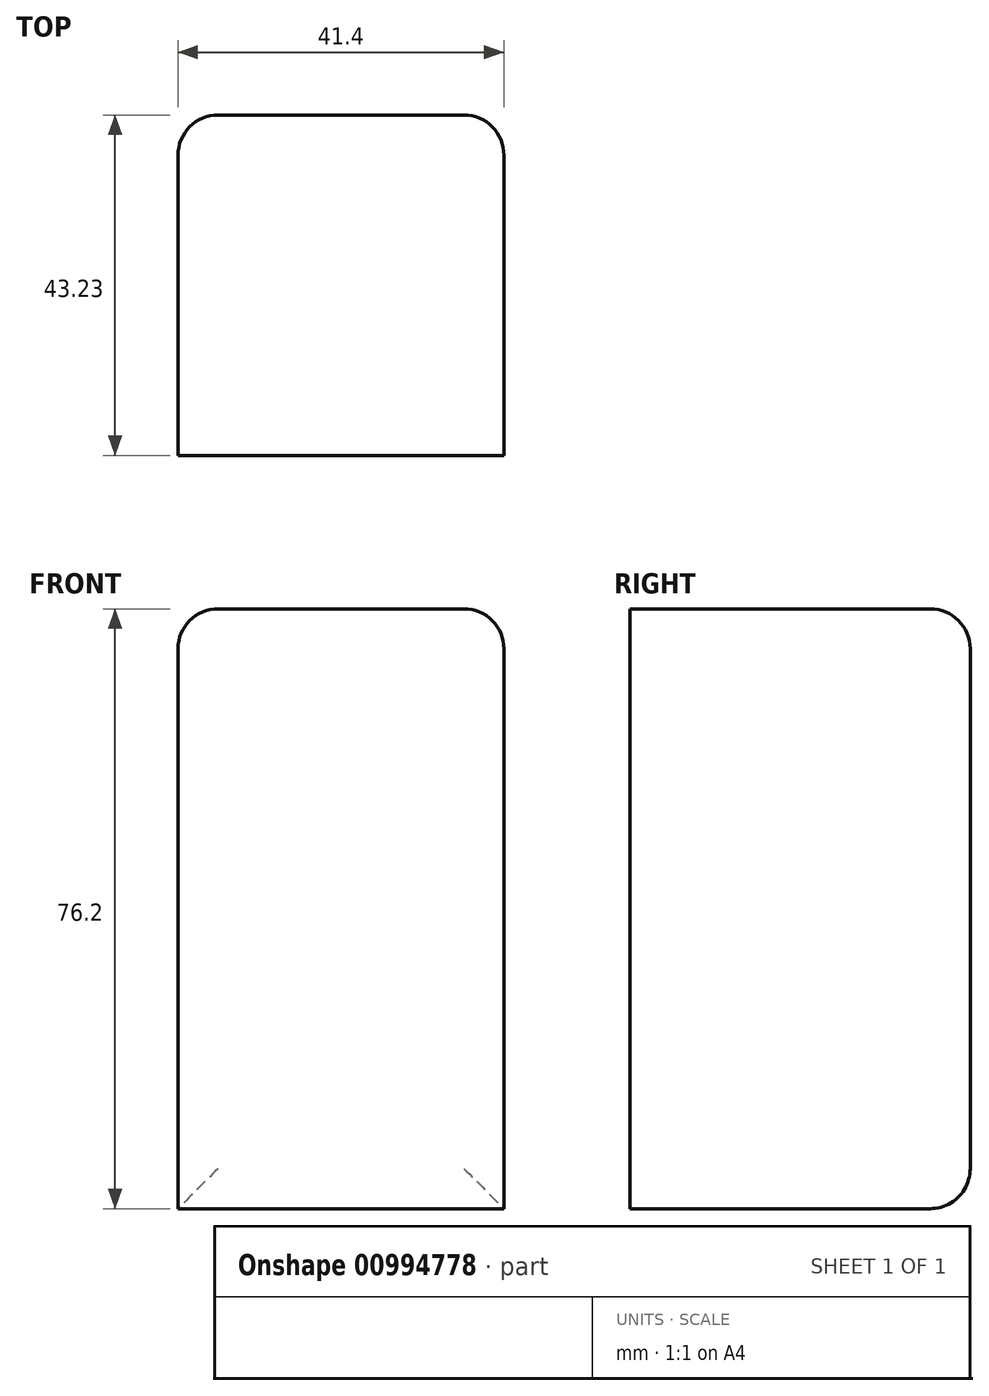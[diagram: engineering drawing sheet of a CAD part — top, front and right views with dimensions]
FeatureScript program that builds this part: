
annotation { "Feature Type Name" : "Feature", "Feature Type Description" : "" }
export const myFeature = defineFeature(function(context is Context, id is Id, definition is map)
    precondition{}
    {
        {
            var Q0;
            Q0=qCreatedBy(makeId("Top.planeOp"),FACE);
            var sketch = newSketch(context, id + "F0", { "sketchPlane" : qUnion([Q0])});
            skLineSegment(sketch, "E0.bottom", {"start": v(0, 56.88) * mm, "end": v(41.4, 56.88) * mm});
            skLineSegment(sketch, "E0.top", {"start": v(0, 13.65) * mm, "end": v(41.4, 13.65) * mm});
            skLineSegment(sketch, "E0.left", {"start": v(0, 56.88) * mm, "end": v(0, 13.65) * mm});
            skLineSegment(sketch, "E0.right", {"start": v(41.4, 56.88) * mm, "end": v(41.4, 13.65) * mm});
            skSolve(sketch);
        }
        {
            var Q0;
            Q0=makeQuery(id+"F0.imprint","IMPRINT",FACE,{"disambiguationData":[TD([[makeQuery(id+"F0.imprint","IMPRINT",EDGE,{"derivedFrom":sQuery(id+"F0.wireOp",EDGE,"E0.bottom")}),-1.0]])]});
            extrude(context, id + "F1", {"entities" : qUnion([Q0]), "depth" : 76.2 * mm, "offsetDistance" : 25.4 * mm});
        }
        {
            var Q0;
            Q0=makeQuery(id+"F1.opExtrude","SWEPT_FACE",FACE,{"disambiguationData":[OSD([sQuery(id+"F0.wireOp",EDGE,"E0.bottom")])]});
            var Q1;
            Q1=makeQuery(id+"F1.opExtrude","CAP_EDGE",EDGE,{"disambiguationData":[OSD([sQuery(id+"F0.wireOp",EDGE,"E0.right")])],"isStart":false});
            var Q2;
            Q2=makeQuery(id+"F1.opExtrude","CAP_EDGE",EDGE,{"disambiguationData":[OSD([sQuery(id+"F0.wireOp",EDGE,"E0.bottom")])],"isStart":false});
            var Q3;
            Q3=makeQuery(id+"F1.opExtrude","CAP_EDGE",EDGE,{"disambiguationData":[OSD([sQuery(id+"F0.wireOp",EDGE,"E0.left")])],"isStart":false});
            fillet(context, id + "F2", {"entities" : qUnion([Q0, Q1, Q2, Q3]), "radius" : 5.08 * mm, "tangentPropagation" : true, "allowEdgeOverflow" : false});
        }
    });
